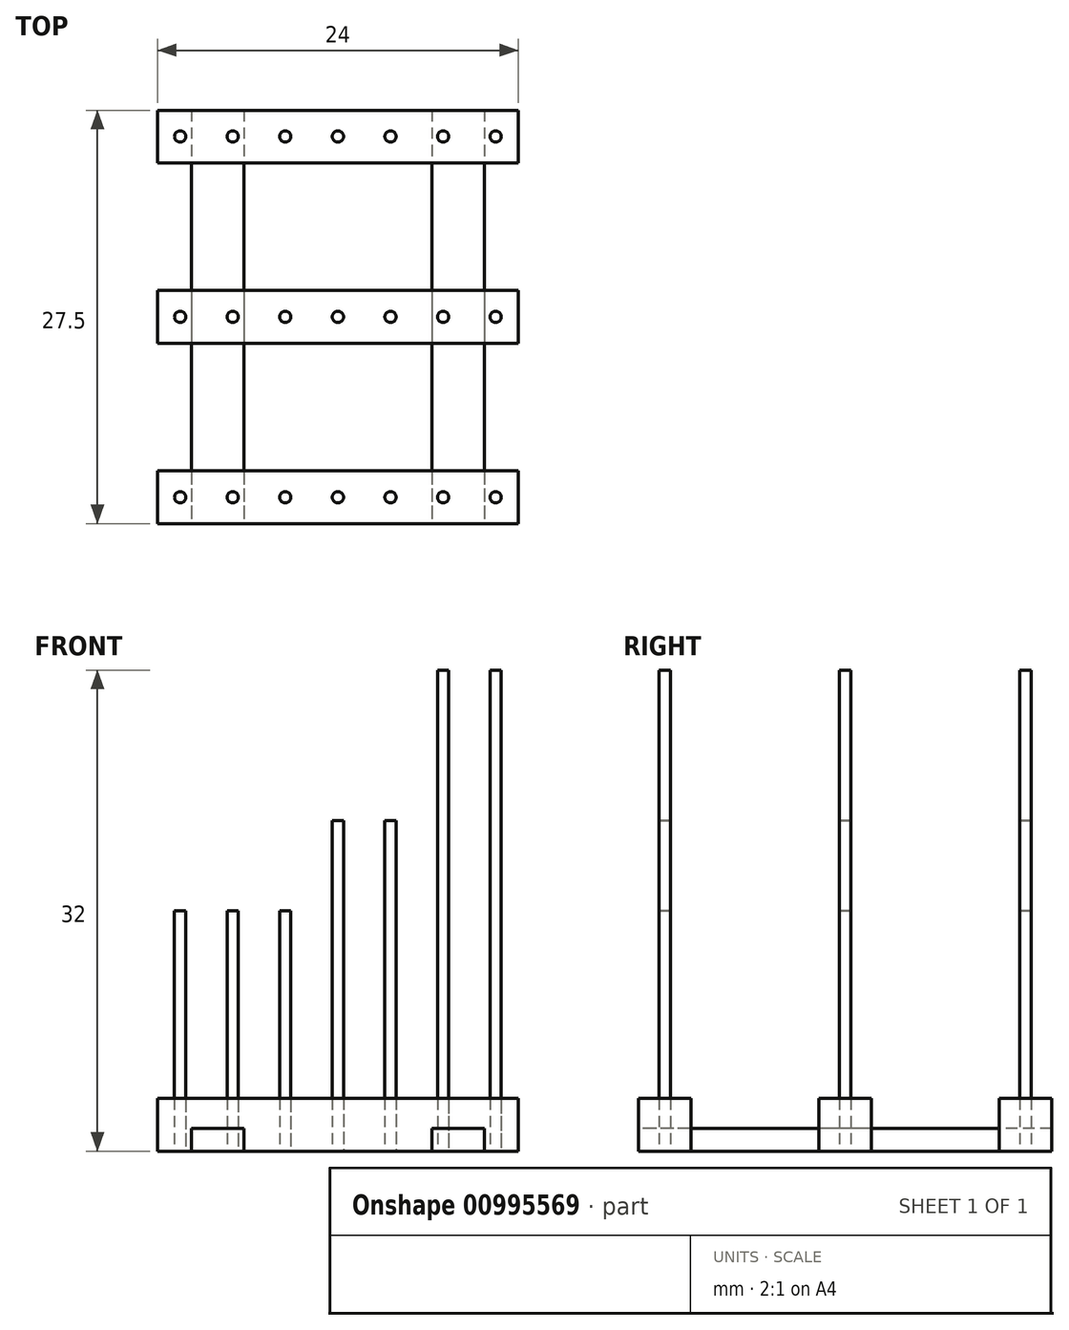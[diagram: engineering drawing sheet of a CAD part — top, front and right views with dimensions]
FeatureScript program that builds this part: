
annotation { "Feature Type Name" : "Feature", "Feature Type Description" : "" }
export const myFeature = defineFeature(function(context is Context, id is Id, definition is map)
    precondition{}
    {
        {
            var Q0;
            Q0=qCreatedBy(makeId("Top.planeOp"),FACE);
            var sketch = newSketch(context, id + "F0", { "sketchPlane" : qUnion([Q0])});
            skLineSegment(sketch, "E0", {"start": v(0, 0) * mm, "end": v(0, 12) * mm, "construction": true});
            skLineSegment(sketch, "E1", {"start": v(0, 0) * mm, "end": v(0, -12) * mm, "construction": true});
            skLineSegment(sketch, "E2.bottom", {"start": v(12, 10.25) * mm, "end": v(-12, 10.25) * mm});
            skLineSegment(sketch, "E2.top", {"start": v(12, 13.75) * mm, "end": v(-12, 13.75) * mm});
            skLineSegment(sketch, "E2.left", {"start": v(12, 10.25) * mm, "end": v(12, 13.75) * mm});
            skLineSegment(sketch, "E2.right", {"start": v(-12, 10.25) * mm, "end": v(-12, 13.75) * mm});
            skPoint(sketch, "E2.middle", {"position": v(0, 12) * mm});
            skLineSegment(sketch, "E3.bottom", {"start": v(12, -1.75) * mm, "end": v(-12, -1.75) * mm});
            skLineSegment(sketch, "E3.top", {"start": v(12, 1.75) * mm, "end": v(-12, 1.75) * mm});
            skLineSegment(sketch, "E3.left", {"start": v(12, -1.75) * mm, "end": v(12, 1.75) * mm});
            skLineSegment(sketch, "E3.right", {"start": v(-12, -1.75) * mm, "end": v(-12, 1.75) * mm});
            skPoint(sketch, "E3.middle", {"position": v(0, 0) * mm});
            skLineSegment(sketch, "E4.bottom", {"start": v(12, -13.75) * mm, "end": v(-12, -13.75) * mm});
            skLineSegment(sketch, "E4.top", {"start": v(12, -10.25) * mm, "end": v(-12, -10.25) * mm});
            skLineSegment(sketch, "E4.left", {"start": v(12, -13.75) * mm, "end": v(12, -10.25) * mm});
            skLineSegment(sketch, "E4.right", {"start": v(-12, -13.75) * mm, "end": v(-12, -10.25) * mm});
            skPoint(sketch, "E4.middle", {"position": v(0, -12) * mm});
            skLineSegment(sketch, "E5", {"start": v(0, 12) * mm, "end": v(-3.5, 12) * mm, "construction": true});
            skLineSegment(sketch, "E6", {"start": v(-3.5, 12) * mm, "end": v(-7, 12) * mm, "construction": true});
            skLineSegment(sketch, "E7", {"start": v(-7, 12) * mm, "end": v(-10.5, 12) * mm, "construction": true});
            skLineSegment(sketch, "E8", {"start": v(0, 12) * mm, "end": v(3.5, 12) * mm, "construction": true});
            skLineSegment(sketch, "E9", {"start": v(3.5, 12) * mm, "end": v(7, 12) * mm, "construction": true});
            skLineSegment(sketch, "E10", {"start": v(7, 12) * mm, "end": v(10.5, 12) * mm, "construction": true});
            skLineSegment(sketch, "E11", {"start": v(0, 0) * mm, "end": v(-3.5, 0) * mm, "construction": true});
            skLineSegment(sketch, "E12", {"start": v(-3.5, 0) * mm, "end": v(-7, 0) * mm, "construction": true});
            skLineSegment(sketch, "E13", {"start": v(-7, 0) * mm, "end": v(-10.5, 0) * mm, "construction": true});
            skLineSegment(sketch, "E14", {"start": v(0, 0) * mm, "end": v(3.5, 0) * mm, "construction": true});
            skLineSegment(sketch, "E15", {"start": v(3.5, 0) * mm, "end": v(7, 0) * mm, "construction": true});
            skLineSegment(sketch, "E16", {"start": v(7, 0) * mm, "end": v(10.5, 0) * mm, "construction": true});
            skLineSegment(sketch, "E17", {"start": v(0, -12) * mm, "end": v(3.5, -12) * mm, "construction": true});
            skLineSegment(sketch, "E18", {"start": v(3.5, -12) * mm, "end": v(7, -12) * mm, "construction": true});
            skLineSegment(sketch, "E19", {"start": v(7, -12) * mm, "end": v(10.5, -12) * mm, "construction": true});
            skLineSegment(sketch, "E20", {"start": v(0, -12) * mm, "end": v(-3.5, -12) * mm, "construction": true});
            skLineSegment(sketch, "E21", {"start": v(-3.5, -12) * mm, "end": v(-7, -12) * mm, "construction": true});
            skLineSegment(sketch, "E22", {"start": v(-7, -12) * mm, "end": v(-10.5, -12) * mm, "construction": true});
            skCircle(sketch, "E23", {"center": v(-3.5, 12) * mm, "radius": 0.38 * mm});
            skCircle(sketch, "E24", {"center": v(-10.5, 12) * mm, "radius": 0.38 * mm});
            skCircle(sketch, "E25", {"center": v(-7, 12) * mm, "radius": 0.38 * mm});
            skCircle(sketch, "E26", {"center": v(0, 12) * mm, "radius": 0.38 * mm});
            skCircle(sketch, "E27", {"center": v(3.5, 12) * mm, "radius": 0.38 * mm});
            skCircle(sketch, "E28", {"center": v(7, 12) * mm, "radius": 0.38 * mm});
            skCircle(sketch, "E29", {"center": v(10.5, 12) * mm, "radius": 0.38 * mm});
            skCircle(sketch, "E30", {"center": v(-10.5, 0) * mm, "radius": 0.38 * mm});
            skCircle(sketch, "E31", {"center": v(-7, 0) * mm, "radius": 0.38 * mm});
            skCircle(sketch, "E32", {"center": v(-3.5, 0) * mm, "radius": 0.38 * mm});
            skCircle(sketch, "E33", {"center": v(3.5, 0) * mm, "radius": 0.38 * mm});
            skCircle(sketch, "E34", {"center": v(0, 0) * mm, "radius": 0.38 * mm});
            skCircle(sketch, "E35", {"center": v(7, 0) * mm, "radius": 0.38 * mm});
            skCircle(sketch, "E36", {"center": v(10.5, 0) * mm, "radius": 0.38 * mm});
            skCircle(sketch, "E37", {"center": v(-10.5, -12) * mm, "radius": 0.38 * mm});
            skCircle(sketch, "E38", {"center": v(-7, -12) * mm, "radius": 0.38 * mm});
            skCircle(sketch, "E39", {"center": v(-3.5, -12) * mm, "radius": 0.38 * mm});
            skCircle(sketch, "E40", {"center": v(0, -12) * mm, "radius": 0.38 * mm});
            skCircle(sketch, "E41", {"center": v(3.5, -12) * mm, "radius": 0.38 * mm});
            skCircle(sketch, "E42", {"center": v(7, -12) * mm, "radius": 0.38 * mm});
            skCircle(sketch, "E43", {"center": v(10.5, -12) * mm, "radius": 0.38 * mm});
            skSolve(sketch);
        }
        {
            var Q0;
            Q0=makeQuery(id+"F0.imprint","IMPRINT",FACE,{"disambiguationData":[TD([[makeQuery(id+"F0.imprint","IMPRINT",EDGE,{"derivedFrom":sQuery(id+"F0.wireOp",EDGE,"E2.bottom")}),-1.0]])]});
            var Q1;
            Q1=makeQuery(id+"F0.imprint","IMPRINT",FACE,{"disambiguationData":[TD([[makeQuery(id+"F0.imprint","IMPRINT",EDGE,{"derivedFrom":sQuery(id+"F0.wireOp",EDGE,"E3.bottom")}),-1.0]])]});
            var Q2;
            Q2=makeQuery(id+"F0.imprint","IMPRINT",FACE,{"disambiguationData":[TD([[makeQuery(id+"F0.imprint","IMPRINT",EDGE,{"derivedFrom":sQuery(id+"F0.wireOp",EDGE,"E4.bottom")}),-1.0]])]});
            extrude(context, id + "F1", {"entities" : qUnion([Q0, Q1, Q2]), "depth" : 3.5 * mm, "offsetDistance" : 25 * mm});
        }
        {
            var Q0;
            Q0=makeQuery(id+"F0.imprint","IMPRINT",FACE,{"disambiguationData":[TD([[makeQuery(id+"F0.imprint","IMPRINT",EDGE,{"derivedFrom":sQuery(id+"F0.wireOp",EDGE,"E24")}),1.0]])]});
            var Q1;
            Q1=makeQuery(id+"F0.imprint","IMPRINT",FACE,{"disambiguationData":[TD([[makeQuery(id+"F0.imprint","IMPRINT",EDGE,{"derivedFrom":sQuery(id+"F0.wireOp",EDGE,"E25")}),1.0]])]});
            var Q2;
            Q2=makeQuery(id+"F0.imprint","IMPRINT",FACE,{"disambiguationData":[TD([[makeQuery(id+"F0.imprint","IMPRINT",EDGE,{"derivedFrom":sQuery(id+"F0.wireOp",EDGE,"E23")}),1.0]])]});
            var Q3;
            Q3=makeQuery(id+"F0.imprint","IMPRINT",FACE,{"disambiguationData":[TD([[makeQuery(id+"F0.imprint","IMPRINT",EDGE,{"derivedFrom":sQuery(id+"F0.wireOp",EDGE,"E30")}),1.0]])]});
            var Q4;
            Q4=makeQuery(id+"F0.imprint","IMPRINT",FACE,{"disambiguationData":[TD([[makeQuery(id+"F0.imprint","IMPRINT",EDGE,{"derivedFrom":sQuery(id+"F0.wireOp",EDGE,"E31")}),1.0]])]});
            var Q5;
            Q5=makeQuery(id+"F0.imprint","IMPRINT",FACE,{"disambiguationData":[TD([[makeQuery(id+"F0.imprint","IMPRINT",EDGE,{"derivedFrom":sQuery(id+"F0.wireOp",EDGE,"E32")}),1.0]])]});
            var Q6;
            Q6=makeQuery(id+"F0.imprint","IMPRINT",FACE,{"disambiguationData":[TD([[makeQuery(id+"F0.imprint","IMPRINT",EDGE,{"derivedFrom":sQuery(id+"F0.wireOp",EDGE,"E39")}),1.0]])]});
            var Q7;
            Q7=makeQuery(id+"F0.imprint","IMPRINT",FACE,{"disambiguationData":[TD([[makeQuery(id+"F0.imprint","IMPRINT",EDGE,{"derivedFrom":sQuery(id+"F0.wireOp",EDGE,"E38")}),1.0]])]});
            var Q8;
            Q8=makeQuery(id+"F0.imprint","IMPRINT",FACE,{"disambiguationData":[TD([[makeQuery(id+"F0.imprint","IMPRINT",EDGE,{"derivedFrom":sQuery(id+"F0.wireOp",EDGE,"E37")}),1.0]])]});
            extrude(context, id + "F2", {"entities" : qUnion([Q0, Q1, Q2, Q3, Q4, Q5, Q6, Q7, Q8]), "depth" : 16 * mm, "offsetDistance" : 25 * mm});
        }
        {
            var Q0;
            Q0=makeQuery(id+"F0.imprint","IMPRINT",FACE,{"disambiguationData":[TD([[makeQuery(id+"F0.imprint","IMPRINT",EDGE,{"derivedFrom":sQuery(id+"F0.wireOp",EDGE,"E26")}),1.0]])]});
            var Q1;
            Q1=makeQuery(id+"F0.imprint","IMPRINT",FACE,{"disambiguationData":[TD([[makeQuery(id+"F0.imprint","IMPRINT",EDGE,{"derivedFrom":sQuery(id+"F0.wireOp",EDGE,"E27")}),1.0]])]});
            var Q2;
            Q2=makeQuery(id+"F0.imprint","IMPRINT",FACE,{"disambiguationData":[TD([[makeQuery(id+"F0.imprint","IMPRINT",EDGE,{"derivedFrom":sQuery(id+"F0.wireOp",EDGE,"E34")}),1.0]])]});
            var Q3;
            Q3=makeQuery(id+"F0.imprint","IMPRINT",FACE,{"disambiguationData":[TD([[makeQuery(id+"F0.imprint","IMPRINT",EDGE,{"derivedFrom":sQuery(id+"F0.wireOp",EDGE,"E33")}),1.0]])]});
            var Q4;
            Q4=makeQuery(id+"F0.imprint","IMPRINT",FACE,{"disambiguationData":[TD([[makeQuery(id+"F0.imprint","IMPRINT",EDGE,{"derivedFrom":sQuery(id+"F0.wireOp",EDGE,"E40")}),1.0]])]});
            var Q5;
            Q5=makeQuery(id+"F0.imprint","IMPRINT",FACE,{"disambiguationData":[TD([[makeQuery(id+"F0.imprint","IMPRINT",EDGE,{"derivedFrom":sQuery(id+"F0.wireOp",EDGE,"E41")}),1.0]])]});
            extrude(context, id + "F3", {"entities" : qUnion([Q0, Q1, Q2, Q3, Q4, Q5]), "depth" : 22 * mm, "offsetDistance" : 25 * mm});
        }
        {
            var Q0;
            Q0=makeQuery(id+"F0.imprint","IMPRINT",FACE,{"disambiguationData":[TD([[makeQuery(id+"F0.imprint","IMPRINT",EDGE,{"derivedFrom":sQuery(id+"F0.wireOp",EDGE,"E28")}),1.0]])]});
            var Q1;
            Q1=makeQuery(id+"F0.imprint","IMPRINT",FACE,{"disambiguationData":[TD([[makeQuery(id+"F0.imprint","IMPRINT",EDGE,{"derivedFrom":sQuery(id+"F0.wireOp",EDGE,"E29")}),1.0]])]});
            var Q2;
            Q2=makeQuery(id+"F0.imprint","IMPRINT",FACE,{"disambiguationData":[TD([[makeQuery(id+"F0.imprint","IMPRINT",EDGE,{"derivedFrom":sQuery(id+"F0.wireOp",EDGE,"E35")}),1.0]])]});
            var Q3;
            Q3=makeQuery(id+"F0.imprint","IMPRINT",FACE,{"disambiguationData":[TD([[makeQuery(id+"F0.imprint","IMPRINT",EDGE,{"derivedFrom":sQuery(id+"F0.wireOp",EDGE,"E36")}),1.0]])]});
            var Q4;
            Q4=makeQuery(id+"F0.imprint","IMPRINT",FACE,{"disambiguationData":[TD([[makeQuery(id+"F0.imprint","IMPRINT",EDGE,{"derivedFrom":sQuery(id+"F0.wireOp",EDGE,"E42")}),1.0]])]});
            var Q5;
            Q5=makeQuery(id+"F0.imprint","IMPRINT",FACE,{"disambiguationData":[TD([[makeQuery(id+"F0.imprint","IMPRINT",EDGE,{"derivedFrom":sQuery(id+"F0.wireOp",EDGE,"E43")}),1.0]])]});
            extrude(context, id + "F4", {"entities" : qUnion([Q0, Q1, Q2, Q3, Q4, Q5]), "depth" : 32 * mm, "offsetDistance" : 25 * mm});
        }
        {
            var Q0;
            Q0=makeQuery(id+"F1.opExtrude","SWEPT_FACE",FACE,{"disambiguationData":[OSD([sQuery(id+"F0.wireOp",EDGE,"E4.bottom")])]});
            var sketch = newSketch(context, id + "F5", { "sketchPlane" : qUnion([Q0])});
            skLineSegment(sketch, "E44", {"start": v(0, 0) * mm, "end": v(-8, 0) * mm});
            skLineSegment(sketch, "E45", {"start": v(0, 0) * mm, "end": v(8, 0) * mm});
            skLineSegment(sketch, "E46.bottom", {"start": v(-6.25, -1.5) * mm, "end": v(-9.75, -1.5) * mm});
            skLineSegment(sketch, "E46.top", {"start": v(-6.25, 1.5) * mm, "end": v(-9.75, 1.5) * mm});
            skLineSegment(sketch, "E46.left", {"start": v(-6.25, -1.5) * mm, "end": v(-6.25, 1.5) * mm});
            skLineSegment(sketch, "E46.right", {"start": v(-9.75, -1.5) * mm, "end": v(-9.75, 1.5) * mm});
            skPoint(sketch, "E46.middle", {"position": v(-8, 0) * mm});
            skLineSegment(sketch, "E47.bottom", {"start": v(9.75, -1.5) * mm, "end": v(6.25, -1.5) * mm});
            skLineSegment(sketch, "E47.top", {"start": v(9.75, 1.5) * mm, "end": v(6.25, 1.5) * mm});
            skLineSegment(sketch, "E47.left", {"start": v(9.75, -1.5) * mm, "end": v(9.75, 1.5) * mm});
            skLineSegment(sketch, "E47.right", {"start": v(6.25, -1.5) * mm, "end": v(6.25, 1.5) * mm});
            skPoint(sketch, "E47.middle", {"position": v(8, 0) * mm});
            skSolve(sketch);
        }
        {
            var Q0;
            {var subQ1=sQuery(id+"F5.wireOp",EDGE,"E46.top");Q0=makeQuery(id+"F5.imprint","IMPRINT",FACE,{"disambiguationData":[TD([[makeQuery(id+"F5.imprint","IMPRINT",EDGE,{"derivedFrom":subQ1}),1.0]])]});}
            var Q1;
            {var subQ1=sQuery(id+"F5.wireOp",EDGE,"E47.top");Q1=makeQuery(id+"F5.imprint","IMPRINT",FACE,{"disambiguationData":[TD([[makeQuery(id+"F5.imprint","IMPRINT",EDGE,{"derivedFrom":subQ1}),1.0]])]});}
            extrude(context, id + "F6", {"entities" : qUnion([Q0, Q1]), "oppositeDirection" : true, "depth" : 27.5 * mm, "offsetDistance" : 25 * mm});
        }
    });
